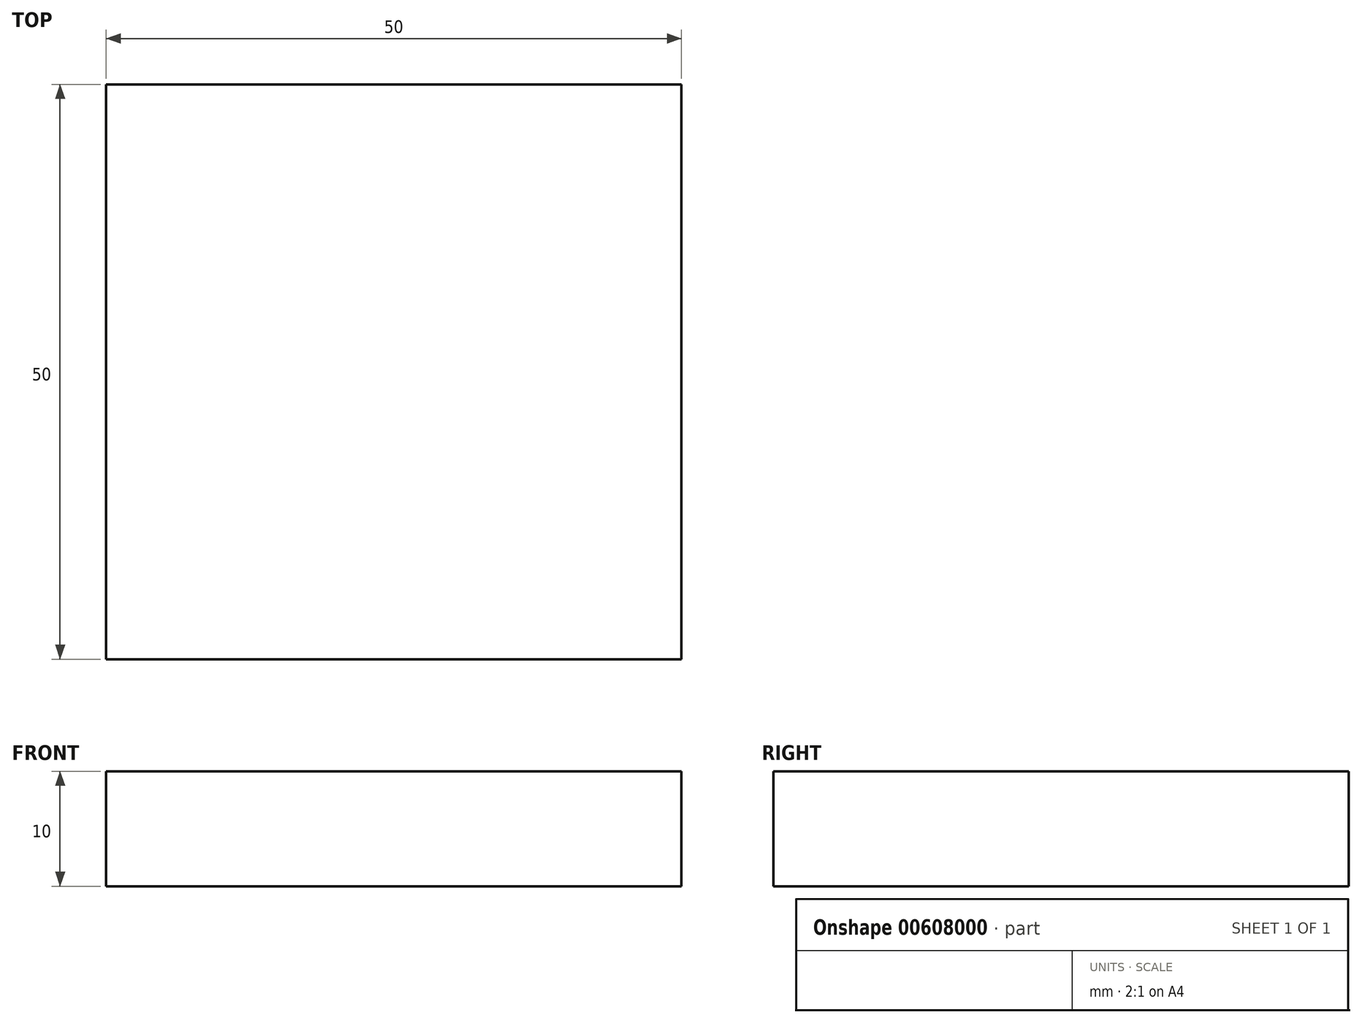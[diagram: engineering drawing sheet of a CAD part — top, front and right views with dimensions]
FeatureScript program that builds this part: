
annotation { "Feature Type Name" : "Feature", "Feature Type Description" : "" }
export const myFeature = defineFeature(function(context is Context, id is Id, definition is map)
    precondition{}
    {
        {
            var Q0;
            Q0=qCreatedBy(makeId("Top.planeOp"),FACE);
            var sketch = newSketch(context, id + "F0", { "sketchPlane" : qUnion([Q0])});
            skLineSegment(sketch, "E0.bottom", {"start": v(25, 25) * mm, "end": v(-25, 25) * mm});
            skLineSegment(sketch, "E0.top", {"start": v(25, -25) * mm, "end": v(-25, -25) * mm});
            skLineSegment(sketch, "E0.left", {"start": v(25, 25) * mm, "end": v(25, -25) * mm});
            skLineSegment(sketch, "E0.right", {"start": v(-25, 25) * mm, "end": v(-25, -25) * mm});
            skPoint(sketch, "E0.middle", {"position": v(0, 0) * mm});
            skSolve(sketch);
        }
        {
            var Q0;
            Q0 = qSketchRegion(id + "F0", true);
            extrude(context, id + "F1", {"entities" : qUnion([Q0]), "depth" : 10 * mm, "offsetDistance" : 25.4 * mm});
        }
    });
